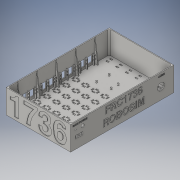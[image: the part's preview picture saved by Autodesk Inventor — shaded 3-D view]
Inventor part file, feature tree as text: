
AUTODESK INVENTOR PART (.ipt)
format: ipt  version: 2016 (Build 200138000, 138)  size: 1,998,848 bytes
history: native  units: in
note: dims shown in document units (in); Inventor stores cm internally (conversion verified against a paired STEP export)
features: extrude x16, sketch x15, chamfer x10, fillet x1
ambient origin geometry x8: Origin, YZ Plane, XZ Plane, XY Plane, X Axis, Y Axis, Z Axis, Center Point
bodies: Solid1 (feature_tree)
feature tree (42):
  extrude  "Extrusion1"  Depth=16.0in
  extrude  "Extrusion2"  Depth=0.2in TaperAngle=0.0deg
  extrude  "Extrusion3"  Depth=3.0in
  chamfer  "Chamfer1"  Distance=3.5in
  chamfer  "Chamfer2"  Distance=0.5in Angle=45.0deg
  chamfer  "Chamfer3"  Distance=0.5in Angle=45.0deg
  chamfer  "Chamfer4"  Distance=0.5in Angle=45.0deg
  chamfer  "Chamfer5"  Distance=0.5in Angle=45.0deg
  chamfer  "Chamfer6"  Distance=0.5in Angle=45.0deg
  chamfer  "Chamfer7"  Distance=0.5in Angle=45.0deg
  chamfer  "Chamfer8"  Distance=0.5in Angle=45.0deg
  chamfer  "Chamfer9"  Distance=0.5in Angle=45.0deg
  extrude  "Extrusion4"  Depth=0.25in TaperAngle=0.0deg
  extrude  "Extrusion6"  Depth=0.075in TaperAngle=0.0deg
  extrude  "Extrusion8"  Depth=0.075in TaperAngle=0.0deg
  extrude  "Extrusion9"  Depth=0.4724in
  extrude  "Extrusion10"  TaperAngle=0.0deg  [1 undecoded]
  extrude  "Extrusion11"  Depth=0.4528in
  extrude  "Extrusion12"  TaperAngle=0.0deg  [1 undecoded]
  extrude  "Extrusion13"  Depth=1.1in
  chamfer  "Chamfer11"  Distance=3.5in Angle=45.0deg
  extrude  "Extrusion14"  Depth=0.125in
  extrude  "Extrusion15"  TaperAngle=0.0deg  [1 undecoded]
  extrude  "Extrusion18"  Depth=3.0in
  extrude  "Extrusion19"  Depth=1.5in TaperAngle=0.0deg
  fillet  "Fillet1"  Radius=12.0in
  sketch  "Sketch1"  dims[d0=10.0in d1=16.0in]
  sketch  "Sketch2"  dims[d2=2.7559in d4=1.5in d5=2.3622in d7=1.5in]
  sketch  "Sketch3"  dims[d11=2.7559in d13=2.3622in d14=2.3622in d16=1.5in d17=0.3937in d19=1.0in d21=0.2in d22=0.0in]
  sketch  "Sketch8"  dims[d23=3.5in d24=0.0in d25=0.7874in d27=9.343in d28=1.9685in d30=3.0in d33=3.5in d34=0.0in d35=0.5in d36=3.5in d37=45.0deg d38=0.5in d39=3.5in d40=45.0deg d41=0.5in d42=3.5in d43=45.0deg d44=0.5in d45=3.5in d46=45.0deg d47=0.5in d48=3.5in d49=45.0deg d50=0.5in d51=3.5in d52=45.0deg d53=0.5in d54=3.5in d55=45.0deg d56=0.5in d57=3.5in d58=45.0deg]
  sketch  "Sketch9"  dims[d59=0.5in d60=3.5in d61=45.0deg d65=0.25in d66=0.0in]
  sketch  "Sketch10"  dims[d69=0.075in d70=0.0in d72=0.0in d73=0.075in]
  sketch  "Sketch11"  dims[d74=0.075in d75=0.0in d76=0.075in d77=0.0in]
  sketch  "Sketch12"  dims[d78=0.1969in d79=0.4724in]
  sketch  "Sketch13"  dims[d80=0.1969in d81=0.0in]
  sketch  "Sketch14"  dims[d82=1.1811in d83=0.4528in]
  sketch  "Sketch15"  dims[d84=0.1969in d85=0.0in]
  sketch  "Sketch16"  dims[d86=0.075in d87=0.0in d88=1.1in]
  sketch  "Sketch17"  dims[d89=0.1969in]
  sketch  "Sketch20"  dims[d90=0.0in d91=0.49in d92=3.5in d93=45.0deg]
  sketch  "Sketch21"  dims[d94=1.5748in d96=3.0in d97=0.3937in d99=1.0in d101=0.1969in d102=0.0in d103=1.5748in d105=3.0in d106=0.3937in d108=1.0in d110=1.5in d111=0.0in d117=12.0in d118=0.0in d119=0.25in d120=0.0in d121=0.125in]
  extrude  "Extrusion7"  Depth=0.25in TaperAngle=0.0deg
note: 3 required parameter values undecoded (feature->parameter linkage not recoverable at this tier; creation-order binding heuristic only, values carry confidence <= 0.55)
